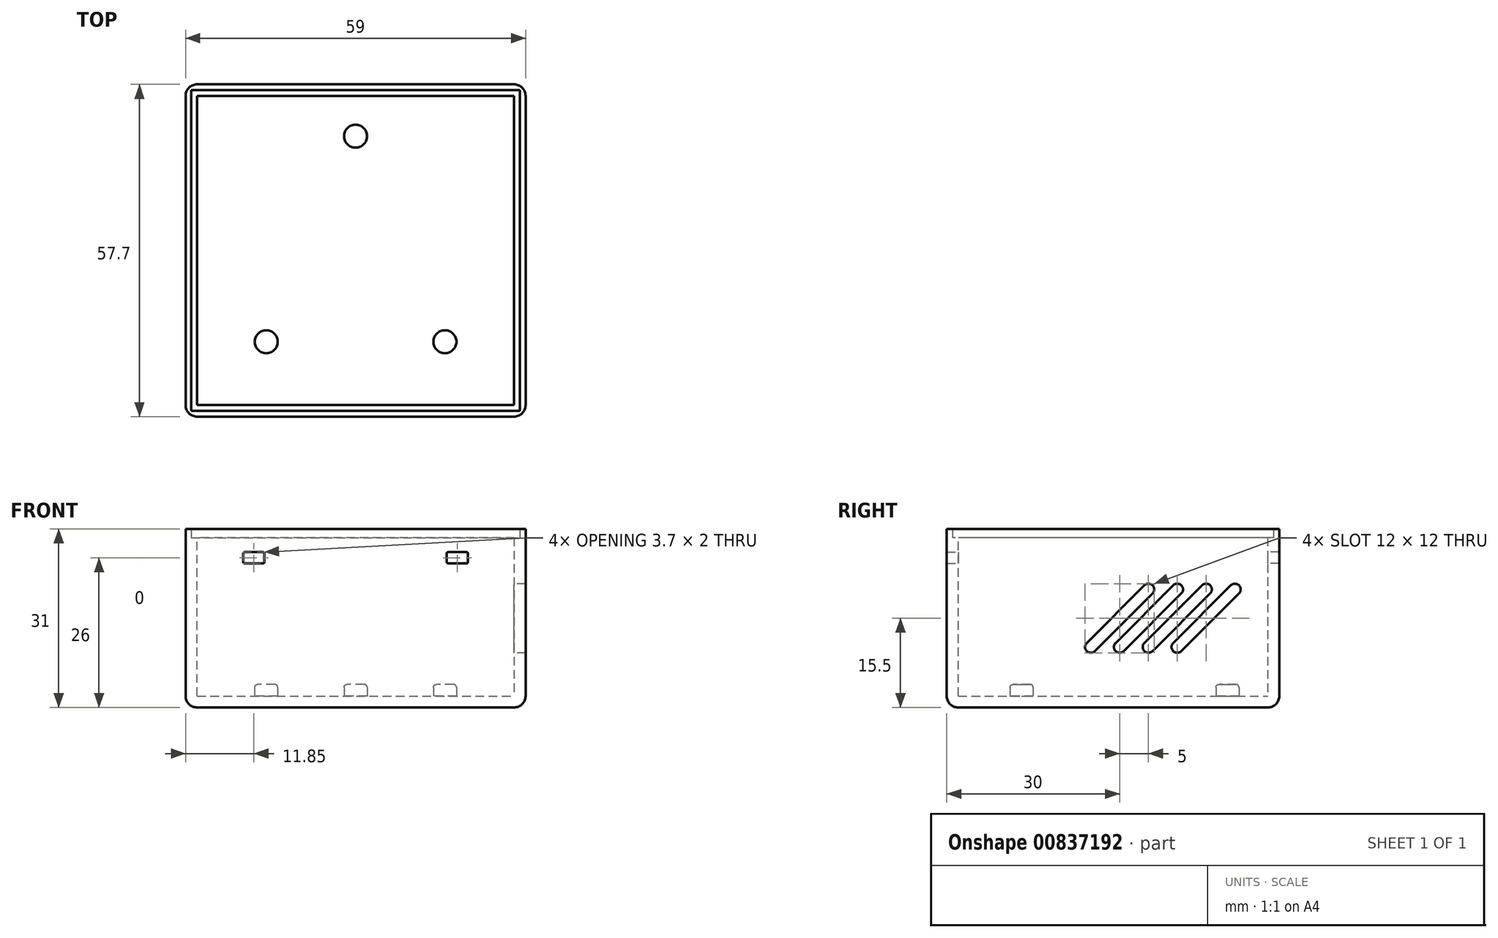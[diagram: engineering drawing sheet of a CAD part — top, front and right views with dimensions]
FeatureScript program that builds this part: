
annotation { "Feature Type Name" : "Feature", "Feature Type Description" : "" }
export const myFeature = defineFeature(function(context is Context, id is Id, definition is map)
    precondition{}
    {
        {
            var Q0;
            Q0=qCreatedBy(makeId("Top.planeOp"),FACE);
            var sketch = newSketch(context, id + "F0", { "sketchPlane" : qUnion([Q0])});
            skLineSegment(sketch, "E0", {"start": v(0, 0) * mm, "end": v(0, 53.7) * mm});
            skLineSegment(sketch, "E1", {"start": v(0, 53.7) * mm, "end": v(55, 53.7) * mm});
            skLineSegment(sketch, "E2", {"start": v(55, 53.7) * mm, "end": v(55, 0) * mm});
            skLineSegment(sketch, "E3", {"start": v(0, 0) * mm, "end": v(55, 0) * mm});
            skPoint(sketch, "E4.visualSharp", {"position": v(0, 53.7) * mm});
            skPoint(sketch, "E5.visualSharp", {"position": v(55, 53.7) * mm});
            skPoint(sketch, "E6.visualSharp", {"position": v(55, 0) * mm});
            skPoint(sketch, "E7.visualSharp", {"position": v(0, 0) * mm});
            skCircle(sketch, "E8", {"center": v(27.5, 46.7) * mm, "radius": 2 * mm});
            skPoint(sketch, "E9", {"position": v(27.5, 53.7) * mm});
            skCircle(sketch, "E10", {"center": v(12, 11) * mm, "radius": 2 * mm});
            skCircle(sketch, "E11", {"center": v(43, 11) * mm, "radius": 2 * mm});
            skLineSegment(sketch, "E12", {"start": v(27.5, 53.7) * mm, "end": v(27.5, 0) * mm, "construction": true});
            skPoint(sketch, "E13", {"position": v(12, 0) * mm});
            skPoint(sketch, "E14", {"position": v(43, 0) * mm});
            skSolve(sketch);
        }
        {
            var Q0;
            Q0=makeQuery(id+"F0.imprint","IMPRINT",FACE,{"disambiguationData":[TD([[makeQuery(id+"F0.imprint","IMPRINT",EDGE,{"derivedFrom":sQuery(id+"F0.wireOp",EDGE,"E0")}),-1.0]])]});
            extrude(context, id + "F1", {"entities" : qUnion([Q0]), "depth" : 2 * mm, "offsetDistance" : 25 * mm});
        }
        {
            var Q0;
            Q0=makeQuery(id+"F0.imprint","IMPRINT",FACE,{"disambiguationData":[TD([[makeQuery(id+"F0.imprint","IMPRINT",EDGE,{"derivedFrom":sQuery(id+"F0.wireOp",EDGE,"E10")}),1.0]])]});
            var Q1;
            Q1=makeQuery(id+"F0.imprint","IMPRINT",FACE,{"disambiguationData":[TD([[makeQuery(id+"F0.imprint","IMPRINT",EDGE,{"derivedFrom":sQuery(id+"F0.wireOp",EDGE,"E8")}),1.0]])]});
            var Q2;
            Q2=makeQuery(id+"F0.imprint","IMPRINT",FACE,{"disambiguationData":[TD([[makeQuery(id+"F0.imprint","IMPRINT",EDGE,{"derivedFrom":sQuery(id+"F0.wireOp",EDGE,"E11")}),1.0]])]});
            extrude(context, id + "F2", {"entities" : qUnion([Q0, Q1, Q2]), "operationType" : NewBodyOperationType.ADD, "depth" : 4 * mm, "offsetDistance" : 25 * mm});
        }
        {
            var Q0;
            Q0=makeQuery(id+"F1.opExtrude","SWEPT_FACE",FACE,{"disambiguationData":[OSD([sQuery(id+"F0.wireOp",EDGE,"E3")])]});
            var sketch = newSketch(context, id + "F3", { "sketchPlane" : qUnion([Q0])});
            skLineSegment(sketch, "E15", {"start": v(0, 0) * mm, "end": v(0, 31) * mm});
            skLineSegment(sketch, "E16", {"start": v(0, 31) * mm, "end": v(55, 31) * mm});
            skLineSegment(sketch, "E17", {"start": v(55, 31) * mm, "end": v(55, 0) * mm});
            skLineSegment(sketch, "E18.bottom", {"start": v(8, 27) * mm, "end": v(11.7, 27) * mm});
            skLineSegment(sketch, "E18.top", {"start": v(8, 25) * mm, "end": v(11.7, 25) * mm});
            skLineSegment(sketch, "E18.left", {"start": v(8, 27) * mm, "end": v(8, 25) * mm});
            skLineSegment(sketch, "E18.right", {"start": v(11.7, 27) * mm, "end": v(11.7, 25) * mm});
            skPoint(sketch, "E19", {"position": v(27.5, 31) * mm});
            skPoint(sketch, "E20", {"position": v(27.5, 0) * mm});
            skLineSegment(sketch, "E21", {"start": v(27.5, 31) * mm, "end": v(27.5, 0) * mm, "construction": true});
            skLineSegment(sketch, "E22.bottom", {"start": v(43.3, 27) * mm, "end": v(47, 27) * mm});
            skLineSegment(sketch, "E22.top", {"start": v(43.3, 25) * mm, "end": v(47, 25) * mm});
            skLineSegment(sketch, "E22.left", {"start": v(47, 27) * mm, "end": v(47, 25) * mm});
            skLineSegment(sketch, "E22.right", {"start": v(43.3, 27) * mm, "end": v(43.3, 25) * mm});
            skPoint(sketch, "E23", {"position": v(55, 29.5) * mm});
            skPoint(sketch, "E24", {"position": v(0, 29.5) * mm});
            skLineSegment(sketch, "E25", {"start": v(0, 29.5) * mm, "end": v(55, 29.5) * mm});
            skSolve(sketch);
        }
        {
            var Q0;
            Q0=makeQuery(id+"F3.imprint","IMPRINT",FACE,{"disambiguationData":[TD([[makeQuery(id+"F3.imprint","IMPRINT",EDGE,{"derivedFrom":sQuery(id+"F3.wireOp",EDGE,"E18.bottom")}),1.0]])]});
            var Q1;
            {var subQ1=sQuery(id+"F0.wireOp",EDGE,"E3");var subQ2=makeQuery(id+"F1.opExtrude","CAP_EDGE",EDGE,{"disambiguationData":[OSD([subQ1])],"isStart":true});Q1=makeQuery(id+"F3.imprint","IMPRINT",FACE,{"disambiguationData":[TD([[makeQuery(id+"F3.imprint","IMPRINT",EDGE,{"derivedFrom":subQ2}),1.0]])]});}
            extrude(context, id + "F4", {"entities" : qUnion([Q0, Q1]), "operationType" : NewBodyOperationType.ADD, "depth" : 2 * mm, "offsetDistance" : 25 * mm});
        }
        {
            var Q0;
            {var subQ0=sQuery(id+"F3.wireOp",EDGE,"E16");Q0=makeQuery(id+"F3.imprint","IMPRINT",FACE,{"disambiguationData":[TD([[makeQuery(id+"F3.imprint","IMPRINT",EDGE,{"derivedFrom":subQ0}),-1.0]])]});}
            extrude(context, id + "F5", {"entities" : qUnion([Q0]), "operationType" : NewBodyOperationType.ADD, "depth" : 2 * mm, "offsetDistance" : 25 * mm, "hasSecondDirection" : true, "secondDirectionOppositeDirection" : true, "secondDirectionDepth" : -1 * mm});
        }
        {
            var Q0;
            {var subQ0=sQuery(id+"F3.wireOp",EDGE,"E17");Q0=makeQuery(id+"F5.boolean.opBoolean","MERGE",FACE,{"derivedFrom":[makeQuery(id+"F4.boolean.opBoolean","MERGE",FACE,{"derivedFrom":[makeQuery(id+"F1.opExtrude","SWEPT_FACE",FACE,{"disambiguationData":[OSD([sQuery(id+"F0.wireOp",EDGE,"E2")])]}),makeQuery(id+"F4.opExtrude","SWEPT_FACE",FACE,{"disambiguationData":[OSD([subQ0])]})]}),makeQuery(id+"F5.opExtrude","SWEPT_FACE",FACE,{"disambiguationData":[OSD([subQ0])]})]});}
            var sketch = newSketch(context, id + "F6", { "sketchPlane" : qUnion([Q0])});
            skLineSegment(sketch, "E26", {"start": v(-2, 0) * mm, "end": v(-2, 31) * mm});
            skLineSegment(sketch, "E27", {"start": v(-2, 31) * mm, "end": v(53.7, 31) * mm});
            skLineSegment(sketch, "E28", {"start": v(53.7, 31) * mm, "end": v(53.7, 0) * mm});
            skPoint(sketch, "E29", {"position": v(53.7, 29.5) * mm});
            skPoint(sketch, "E30", {"position": v(-2, 29.5) * mm});
            skLineSegment(sketch, "E31", {"start": v(-2, 29.5) * mm, "end": v(53.7, 29.5) * mm});
            skCircle(sketch, "E32", {"center": v(23, 10.5) * mm, "radius": 1 * mm});
            skLineSegment(sketch, "E33.top", {"start": v(23, 20.5) * mm, "end": v(33, 20.5) * mm, "construction": true});
            skLineSegment(sketch, "E33.left", {"start": v(23, 10.5) * mm, "end": v(23, 20.5) * mm, "construction": true});
            skCircle(sketch, "E34", {"center": v(33, 20.5) * mm, "radius": 1 * mm});
            skLineSegment(sketch, "E35", {"start": v(22.3, 11.2) * mm, "end": v(32.3, 21.2) * mm});
            skLineSegment(sketch, "E36", {"start": v(23.7, 9.8) * mm, "end": v(33.7, 19.8) * mm});
            skCircle(sketch, "E37", {"center": v(28, 10.5) * mm, "radius": 1 * mm});
            skCircle(sketch, "E38", {"center": v(38, 20.5) * mm, "radius": 1 * mm});
            skLineSegment(sketch, "E39", {"start": v(27.3, 11.2) * mm, "end": v(37.3, 21.2) * mm});
            skLineSegment(sketch, "E40", {"start": v(28.7, 9.8) * mm, "end": v(38.7, 19.8) * mm});
            skCircle(sketch, "E41", {"center": v(33, 10.5) * mm, "radius": 1 * mm});
            skCircle(sketch, "E42", {"center": v(43, 20.5) * mm, "radius": 1 * mm});
            skLineSegment(sketch, "E43", {"start": v(32.3, 11.2) * mm, "end": v(42.3, 21.2) * mm});
            skLineSegment(sketch, "E44", {"start": v(33.7, 9.8) * mm, "end": v(43.7, 19.8) * mm});
            skLineSegment(sketch, "E45", {"start": v(23, 10.5) * mm, "end": v(28, 10.5) * mm, "construction": true});
            skLineSegment(sketch, "E46", {"start": v(28, 10.5) * mm, "end": v(33, 10.5) * mm, "construction": true});
            skCircle(sketch, "E47", {"center": v(38, 10.5) * mm, "radius": 1 * mm});
            skCircle(sketch, "E48", {"center": v(48, 20.5) * mm, "radius": 1 * mm});
            skLineSegment(sketch, "E49", {"start": v(37.3, 11.2) * mm, "end": v(47.3, 21.2) * mm});
            skLineSegment(sketch, "E50", {"start": v(38.7, 9.8) * mm, "end": v(48.7, 19.8) * mm});
            skLineSegment(sketch, "E51", {"start": v(33, 10.5) * mm, "end": v(38, 10.5) * mm, "construction": true});
            skLineSegment(sketch, "E52", {"start": v(33, 20.5) * mm, "end": v(33, 31) * mm, "construction": true});
            skLineSegment(sketch, "E53", {"start": v(23, 10.5) * mm, "end": v(23, 0) * mm, "construction": true});
            skSolve(sketch);
        }
        {
            var Q0;
            {var subQ6=sQuery(id+"F0.wireOp",EDGE,"E2");var subQ9=makeQuery(id+"F1.opExtrude","CAP_EDGE",EDGE,{"disambiguationData":[OSD([subQ6])],"isStart":false});Q0=makeQuery(id+"F6.imprint","IMPRINT",FACE,{"disambiguationData":[TD([[makeQuery(id+"F6.imprint","IMPRINT",EDGE,{"derivedFrom":subQ9}),1.0]])]});}
            var Q1;
            {var subQ2=sQuery(id+"F6.wireOp",EDGE,"E35");Q1=makeQuery(id+"F6.imprint","IMPRINT",FACE,{"disambiguationData":[TD([[makeQuery(id+"F6.imprint","IMPRINT",EDGE,{"derivedFrom":subQ2}),1.0]])]});}
            extrude(context, id + "F7", {"entities" : qUnion([Q0, Q1]), "operationType" : NewBodyOperationType.ADD, "depth" : 2 * mm, "offsetDistance" : 25 * mm});
        }
        {
            var Q0;
            {var subQ1=sQuery(id+"F3.wireOp",EDGE,"E17");var subQ5=makeQuery(id+"F5.opExtrude","CAP_EDGE",EDGE,{"disambiguationData":[OSD([subQ1])],"isStart":true});Q0=makeQuery(id+"F6.imprint","IMPRINT",FACE,{"disambiguationData":[TD([[makeQuery(id+"F6.imprint","IMPRINT",EDGE,{"derivedFrom":subQ5}),1.0]])]});}
            extrude(context, id + "F8", {"entities" : qUnion([Q0]), "operationType" : NewBodyOperationType.ADD, "depth" : 2 * mm, "offsetDistance" : 25 * mm, "hasSecondDirection" : true, "secondDirectionOppositeDirection" : true, "secondDirectionDepth" : -1 * mm});
        }
        {
            var Q0;
            Q0=makeQuery(id+"F7.boolean.opBoolean","MERGE",FACE,{"derivedFrom":[makeQuery(id+"F4.opExtrude","SWEPT_FACE",FACE,{"disambiguationData":[OSD([sQuery(id+"F3.wireOp",EDGE,"E25")])]}),makeQuery(id+"F7.opExtrude","SWEPT_FACE",FACE,{"disambiguationData":[OSD([sQuery(id+"F6.wireOp",EDGE,"E31")])]})]});
            var sketch = newSketch(context, id + "F9", { "sketchPlane" : qUnion([Q0])});
            skLineSegment(sketch, "E54", {"start": v(55, -1) * mm, "end": v(56, -1) * mm});
            skSolve(sketch);
        }
        {
            var Q0;
            Q0=makeQuery(id+"F9.imprint","IMPRINT",FACE,{"disambiguationData":[TD([[makeQuery(id+"F9.imprint","IMPRINT",EDGE,{"derivedFrom":sQuery(id+"F9.wireOp",EDGE,"E54")}),-1.0]])]});
            extrude(context, id + "F10", {"entities" : qUnion([Q0]), "operationType" : NewBodyOperationType.ADD, "depth" : 1.5 * mm, "offsetDistance" : 25 * mm});
        }
        {
            var Q0;
            {var subQ0=sQuery(id+"F6.wireOp",EDGE,"E28");Q0=makeQuery(id+"F8.boolean.opBoolean","MERGE",FACE,{"derivedFrom":[makeQuery(id+"F7.boolean.opBoolean","MERGE",FACE,{"derivedFrom":[makeQuery(id+"F1.opExtrude","SWEPT_FACE",FACE,{"disambiguationData":[OSD([sQuery(id+"F0.wireOp",EDGE,"E1")])]}),makeQuery(id+"F7.opExtrude","SWEPT_FACE",FACE,{"disambiguationData":[OSD([subQ0])]})]}),makeQuery(id+"F8.opExtrude","SWEPT_FACE",FACE,{"disambiguationData":[OSD([subQ0])]})]});}
            var sketch = newSketch(context, id + "F11", { "sketchPlane" : qUnion([Q0])});
            skLineSegment(sketch, "E55", {"start": v(-57, 0) * mm, "end": v(-57, 31) * mm});
            skLineSegment(sketch, "E56", {"start": v(-57, 0) * mm, "end": v(0, 0) * mm});
            skLineSegment(sketch, "E57", {"start": v(-57, 31) * mm, "end": v(0, 31) * mm});
            skLineSegment(sketch, "E58", {"start": v(0, 31) * mm, "end": v(0, 0) * mm});
            skPoint(sketch, "E59", {"position": v(0, 29.5) * mm});
            skPoint(sketch, "E60", {"position": v(-57, 29.5) * mm});
            skLineSegment(sketch, "E61", {"start": v(-57, 29.5) * mm, "end": v(0, 29.5) * mm});
            skPoint(sketch, "E62", {"position": v(-27.5, 2) * mm});
            skLineSegment(sketch, "E63", {"start": v(-27.5, 2) * mm, "end": v(-27.5, 29.5) * mm, "construction": true});
            skLineSegment(sketch, "E64.bottom", {"start": v(-47, 27) * mm, "end": v(-43.3, 27) * mm});
            skLineSegment(sketch, "E64.top", {"start": v(-47, 25) * mm, "end": v(-43.3, 25) * mm});
            skLineSegment(sketch, "E64.left", {"start": v(-47, 27) * mm, "end": v(-47, 25) * mm});
            skLineSegment(sketch, "E64.right", {"start": v(-43.3, 27) * mm, "end": v(-43.3, 25) * mm});
            skLineSegment(sketch, "E65.bottom", {"start": v(-11.7, 27) * mm, "end": v(-8, 27) * mm});
            skLineSegment(sketch, "E65.top", {"start": v(-11.7, 25) * mm, "end": v(-8, 25) * mm});
            skLineSegment(sketch, "E65.left", {"start": v(-11.7, 27) * mm, "end": v(-11.7, 25) * mm});
            skLineSegment(sketch, "E65.right", {"start": v(-8, 27) * mm, "end": v(-8, 25) * mm});
            skSolve(sketch);
        }
        {
            var Q0;
            Q0=makeQuery(id+"F11.imprint","IMPRINT",FACE,{"disambiguationData":[TD([[makeQuery(id+"F11.imprint","IMPRINT",EDGE,{"derivedFrom":sQuery(id+"F11.wireOp",EDGE,"E64.bottom")}),1.0]])]});
            var Q1;
            {var subQ7=sQuery(id+"F11.wireOp",EDGE,"E56");Q1=makeQuery(id+"F11.imprint","IMPRINT",FACE,{"disambiguationData":[TD([[makeQuery(id+"F11.imprint","IMPRINT",EDGE,{"derivedFrom":subQ7}),-1.0]])]});}
            extrude(context, id + "F12", {"entities" : qUnion([Q0, Q1]), "operationType" : NewBodyOperationType.ADD, "depth" : 2 * mm, "offsetDistance" : 25 * mm});
        }
        {
            var Q0;
            {var subQ1=sQuery(id+"F6.wireOp",EDGE,"E28");var subQ5=makeQuery(id+"F8.opExtrude","CAP_EDGE",EDGE,{"disambiguationData":[OSD([subQ1])],"isStart":true});Q0=makeQuery(id+"F11.imprint","IMPRINT",FACE,{"disambiguationData":[TD([[makeQuery(id+"F11.imprint","IMPRINT",EDGE,{"derivedFrom":subQ5}),1.0]])]});}
            extrude(context, id + "F13", {"entities" : qUnion([Q0]), "operationType" : NewBodyOperationType.ADD, "depth" : 2 * mm, "offsetDistance" : 25 * mm, "hasSecondDirection" : true, "secondDirectionOppositeDirection" : true, "secondDirectionDepth" : -1 * mm});
        }
        {
            var Q0;
            Q0=makeQuery(id+"F12.boolean.opBoolean","MERGE",FACE,{"derivedFrom":[makeQuery(id+"F7.boolean.opBoolean","MERGE",FACE,{"derivedFrom":[makeQuery(id+"F4.opExtrude","SWEPT_FACE",FACE,{"disambiguationData":[OSD([sQuery(id+"F3.wireOp",EDGE,"E25")])]}),makeQuery(id+"F7.opExtrude","SWEPT_FACE",FACE,{"disambiguationData":[OSD([sQuery(id+"F6.wireOp",EDGE,"E31")])]})]}),makeQuery(id+"F12.opExtrude","SWEPT_FACE",FACE,{"disambiguationData":[OSD([sQuery(id+"F11.wireOp",EDGE,"E61")])]})]});
            var sketch = newSketch(context, id + "F14", { "sketchPlane" : qUnion([Q0])});
            skLineSegment(sketch, "E66", {"start": v(56, 53.7) * mm, "end": v(56, 55.7) * mm});
            skLineSegment(sketch, "E67", {"start": v(56, 55.7) * mm, "end": v(57, 55.7) * mm});
            skLineSegment(sketch, "E68", {"start": v(57, 55.7) * mm, "end": v(57, 53.7) * mm});
            skLineSegment(sketch, "E69", {"start": v(57, 53.7) * mm, "end": v(56, 53.7) * mm});
            skSolve(sketch);
        }
        {
            var Q0;
            {var subQ0=sQuery(id+"F14.wireOp",EDGE,"E67");Q0=makeQuery(id+"F14.imprint","IMPRINT",FACE,{"disambiguationData":[TD([[makeQuery(id+"F14.imprint","IMPRINT",EDGE,{"derivedFrom":subQ0}),1.0]])]});}
            extrude(context, id + "F15", {"entities" : qUnion([Q0]), "operationType" : NewBodyOperationType.ADD, "depth" : 1.5 * mm, "offsetDistance" : 25 * mm});
        }
        {
            var Q0;
            {var subQ0=sQuery(id+"F11.wireOp",EDGE,"E58");var subQ1=sQuery(id+"F3.wireOp",EDGE,"E15");var subQ2=sQuery(id+"F0.wireOp",EDGE,"E3");Q0=makeQuery(id+"F13.boolean.opBoolean","MERGE",FACE,{"derivedFrom":[makeQuery(id+"F12.boolean.opBoolean","MERGE",FACE,{"derivedFrom":[makeQuery(id+"F4.boolean.opBoolean","MERGE",FACE,{"derivedFrom":[makeQuery(id+"F1.opExtrude","SWEPT_FACE",FACE,{"disambiguationData":[OSD([sQuery(id+"F0.wireOp",EDGE,"E0")])]}),makeQuery(id+"F4.opExtrude","SWEPT_FACE",FACE,{"disambiguationData":[OSD([subQ1]),TDD([makeQuery(id+"F3.imprint","IMPRINT",EDGE,{"disambiguationData":[TD([[makeQuery(id+"F3.imprint","INTERSECT",VERTEX,{"derivedFrom":[makeQuery(id+"F1.opExtrude","CAP_EDGE",EDGE,{"disambiguationData":[OSD([subQ2])],"isStart":true}),subQ1]}),1.0]])],"derivedFrom":subQ1})])]})]}),makeQuery(id+"F12.opExtrude","SWEPT_FACE",FACE,{"disambiguationData":[OSD([subQ0])]})]}),makeQuery(id+"F13.opExtrude","SWEPT_FACE",FACE,{"disambiguationData":[OSD([subQ0])]})]});}
            var sketch = newSketch(context, id + "F16", { "sketchPlane" : qUnion([Q0])});
            skLineSegment(sketch, "E70", {"start": v(-55.7, 0) * mm, "end": v(2, 0) * mm});
            skLineSegment(sketch, "E71", {"start": v(2, 0) * mm, "end": v(2, 31) * mm});
            skLineSegment(sketch, "E72", {"start": v(2, 31) * mm, "end": v(-55.7, 31) * mm});
            skLineSegment(sketch, "E73", {"start": v(-55.7, 31) * mm, "end": v(-55.7, 0) * mm});
            skPoint(sketch, "E74", {"position": v(-55.7, 29.5) * mm});
            skPoint(sketch, "E75", {"position": v(2, 29.5) * mm});
            skLineSegment(sketch, "E76", {"start": v(-55.7, 29.5) * mm, "end": v(2, 29.5) * mm});
            skSolve(sketch);
        }
        {
            var Q0;
            Q0=makeQuery(id+"F16.imprint","IMPRINT",FACE,{"disambiguationData":[TD([[makeQuery(id+"F16.imprint","IMPRINT",EDGE,{"derivedFrom":makeQuery(id+"F1.opExtrude","CAP_EDGE",EDGE,{"disambiguationData":[OSD([sQuery(id+"F0.wireOp",EDGE,"E0")])],"isStart":false})}),-1.0]])]});
            var Q1;
            Q1=makeQuery(id+"F16.imprint","IMPRINT",FACE,{"disambiguationData":[TD([[makeQuery(id+"F16.imprint","IMPRINT",EDGE,{"derivedFrom":makeQuery(id+"F1.opExtrude","CAP_EDGE",EDGE,{"disambiguationData":[OSD([sQuery(id+"F0.wireOp",EDGE,"E0")])],"isStart":false})}),1.0]])]});
            extrude(context, id + "F17", {"entities" : qUnion([Q0, Q1]), "operationType" : NewBodyOperationType.ADD, "depth" : 2 * mm, "offsetDistance" : 25 * mm});
        }
        {
            var Q0;
            {var subQ1=sQuery(id+"F11.wireOp",EDGE,"E58");var subQ3=makeQuery(id+"F13.opExtrude","CAP_EDGE",EDGE,{"disambiguationData":[OSD([subQ1])],"isStart":true});Q0=makeQuery(id+"F16.imprint","IMPRINT",FACE,{"disambiguationData":[TD([[makeQuery(id+"F16.imprint","IMPRINT",EDGE,{"derivedFrom":subQ3}),1.0]])]});}
            extrude(context, id + "F18", {"entities" : qUnion([Q0]), "operationType" : NewBodyOperationType.ADD, "depth" : 2 * mm, "offsetDistance" : 25 * mm, "hasSecondDirection" : true, "secondDirectionOppositeDirection" : true, "secondDirectionDepth" : -1 * mm});
        }
        {
            var Q0;
            Q0=makeQuery(id+"F17.boolean.opBoolean","MERGE",FACE,{"derivedFrom":[makeQuery(id+"F12.boolean.opBoolean","MERGE",FACE,{"derivedFrom":[makeQuery(id+"F7.boolean.opBoolean","MERGE",FACE,{"derivedFrom":[makeQuery(id+"F4.opExtrude","SWEPT_FACE",FACE,{"disambiguationData":[OSD([sQuery(id+"F3.wireOp",EDGE,"E25")])]}),makeQuery(id+"F7.opExtrude","SWEPT_FACE",FACE,{"disambiguationData":[OSD([sQuery(id+"F6.wireOp",EDGE,"E31")])]})]}),makeQuery(id+"F12.opExtrude","SWEPT_FACE",FACE,{"disambiguationData":[OSD([sQuery(id+"F11.wireOp",EDGE,"E61")])]})]}),makeQuery(id+"F17.opExtrude","SWEPT_FACE",FACE,{"disambiguationData":[OSD([sQuery(id+"F16.wireOp",EDGE,"E76")])]})]});
            var sketch = newSketch(context, id + "F19", { "sketchPlane" : qUnion([Q0])});
            skLineSegment(sketch, "E77", {"start": v(0, 55.7) * mm, "end": v(0, 54.7) * mm});
            skLineSegment(sketch, "E78", {"start": v(0, 54.7) * mm, "end": v(-2, 54.7) * mm});
            skLineSegment(sketch, "E79", {"start": v(-2, 54.7) * mm, "end": v(-2, 55.7) * mm});
            skLineSegment(sketch, "E80", {"start": v(-2, 55.7) * mm, "end": v(0, 55.7) * mm});
            skSolve(sketch);
        }
        {
            var Q0;
            {var subQ3=sQuery(id+"F19.wireOp",EDGE,"E77");Q0=makeQuery(id+"F19.imprint","IMPRINT",FACE,{"disambiguationData":[TD([[makeQuery(id+"F19.imprint","IMPRINT",EDGE,{"derivedFrom":subQ3}),-1.0]])]});}
            extrude(context, id + "F20", {"entities" : qUnion([Q0]), "operationType" : NewBodyOperationType.ADD, "depth" : 1.5 * mm, "offsetDistance" : 25 * mm});
        }
        {
            var Q0;
            Q0=makeQuery(id+"F17.boolean.opBoolean","MERGE",FACE,{"derivedFrom":[makeQuery(id+"F12.boolean.opBoolean","MERGE",FACE,{"derivedFrom":[makeQuery(id+"F7.boolean.opBoolean","MERGE",FACE,{"derivedFrom":[makeQuery(id+"F4.opExtrude","SWEPT_FACE",FACE,{"disambiguationData":[OSD([sQuery(id+"F3.wireOp",EDGE,"E25")])]}),makeQuery(id+"F7.opExtrude","SWEPT_FACE",FACE,{"disambiguationData":[OSD([sQuery(id+"F6.wireOp",EDGE,"E31")])]})]}),makeQuery(id+"F12.opExtrude","SWEPT_FACE",FACE,{"disambiguationData":[OSD([sQuery(id+"F11.wireOp",EDGE,"E61")])]})]}),makeQuery(id+"F17.opExtrude","SWEPT_FACE",FACE,{"disambiguationData":[OSD([sQuery(id+"F16.wireOp",EDGE,"E76")])]})]});
            var sketch = newSketch(context, id + "F21", { "sketchPlane" : qUnion([Q0])});
            skLineSegment(sketch, "E81", {"start": v(0, -2) * mm, "end": v(-1, -2) * mm});
            skLineSegment(sketch, "E82", {"start": v(-1, -2) * mm, "end": v(-1, -1) * mm});
            skLineSegment(sketch, "E83", {"start": v(-1, -1) * mm, "end": v(0, -1) * mm});
            skLineSegment(sketch, "E84", {"start": v(0, -1) * mm, "end": v(0, -2) * mm});
            skSolve(sketch);
        }
        {
            var Q0;
            Q0=makeQuery(id+"F21.imprint","IMPRINT",FACE,{"disambiguationData":[TD([[makeQuery(id+"F21.imprint","IMPRINT",EDGE,{"derivedFrom":sQuery(id+"F21.wireOp",EDGE,"E81")}),1.0]])]});
            extrude(context, id + "F22", {"entities" : qUnion([Q0]), "operationType" : NewBodyOperationType.ADD, "depth" : 1.5 * mm, "offsetDistance" : 25 * mm});
        }
        {
            var Q0;
            Q0=makeQuery(id+"F4.opExtrude","SWEPT_EDGE",EDGE,{"disambiguationData":[OSD([sQuery(id+"F3.wireOp",EDGE,"E18.bottom"),sQuery(id+"F3.wireOp",EDGE,"E18.left")])]});
            var Q1;
            Q1=makeQuery(id+"F4.opExtrude","SWEPT_EDGE",EDGE,{"disambiguationData":[OSD([sQuery(id+"F3.wireOp",EDGE,"E18.bottom"),sQuery(id+"F3.wireOp",EDGE,"E18.right")])]});
            var Q2;
            Q2=makeQuery(id+"F4.opExtrude","SWEPT_EDGE",EDGE,{"disambiguationData":[OSD([sQuery(id+"F3.wireOp",EDGE,"E18.top"),sQuery(id+"F3.wireOp",EDGE,"E18.left")])]});
            var Q3;
            Q3=makeQuery(id+"F4.opExtrude","SWEPT_EDGE",EDGE,{"disambiguationData":[OSD([sQuery(id+"F3.wireOp",EDGE,"E18.top"),sQuery(id+"F3.wireOp",EDGE,"E18.right")])]});
            var Q4;
            Q4=makeQuery(id+"F4.opExtrude","SWEPT_EDGE",EDGE,{"disambiguationData":[OSD([sQuery(id+"F3.wireOp",EDGE,"E22.top"),sQuery(id+"F3.wireOp",EDGE,"E22.right")])]});
            var Q5;
            Q5=makeQuery(id+"F4.opExtrude","SWEPT_EDGE",EDGE,{"disambiguationData":[OSD([sQuery(id+"F3.wireOp",EDGE,"E22.top"),sQuery(id+"F3.wireOp",EDGE,"E22.left")])]});
            var Q6;
            Q6=makeQuery(id+"F4.opExtrude","SWEPT_EDGE",EDGE,{"disambiguationData":[OSD([sQuery(id+"F3.wireOp",EDGE,"E22.bottom"),sQuery(id+"F3.wireOp",EDGE,"E22.right")])]});
            var Q7;
            Q7=makeQuery(id+"F4.opExtrude","SWEPT_EDGE",EDGE,{"disambiguationData":[OSD([sQuery(id+"F3.wireOp",EDGE,"E22.bottom"),sQuery(id+"F3.wireOp",EDGE,"E22.left")])]});
            var Q8;
            Q8=makeQuery(id+"F12.opExtrude","SWEPT_EDGE",EDGE,{"disambiguationData":[OSD([sQuery(id+"F11.wireOp",EDGE,"E64.bottom"),sQuery(id+"F11.wireOp",EDGE,"E64.left")])]});
            var Q9;
            Q9=makeQuery(id+"F12.opExtrude","SWEPT_EDGE",EDGE,{"disambiguationData":[OSD([sQuery(id+"F11.wireOp",EDGE,"E64.top"),sQuery(id+"F11.wireOp",EDGE,"E64.right")])]});
            var Q10;
            Q10=makeQuery(id+"F12.opExtrude","SWEPT_EDGE",EDGE,{"disambiguationData":[OSD([sQuery(id+"F11.wireOp",EDGE,"E64.bottom"),sQuery(id+"F11.wireOp",EDGE,"E64.right")])]});
            var Q11;
            Q11=makeQuery(id+"F12.opExtrude","SWEPT_EDGE",EDGE,{"disambiguationData":[OSD([sQuery(id+"F11.wireOp",EDGE,"E64.top"),sQuery(id+"F11.wireOp",EDGE,"E64.left")])]});
            var Q12;
            Q12=makeQuery(id+"F12.opExtrude","SWEPT_EDGE",EDGE,{"disambiguationData":[OSD([sQuery(id+"F11.wireOp",EDGE,"E65.top"),sQuery(id+"F11.wireOp",EDGE,"E65.left")])]});
            var Q13;
            Q13=makeQuery(id+"F12.opExtrude","SWEPT_EDGE",EDGE,{"disambiguationData":[OSD([sQuery(id+"F11.wireOp",EDGE,"E65.top"),sQuery(id+"F11.wireOp",EDGE,"E65.right")])]});
            var Q14;
            Q14=makeQuery(id+"F12.opExtrude","SWEPT_EDGE",EDGE,{"disambiguationData":[OSD([sQuery(id+"F11.wireOp",EDGE,"E65.bottom"),sQuery(id+"F11.wireOp",EDGE,"E65.left")])]});
            var Q15;
            Q15=makeQuery(id+"F12.opExtrude","SWEPT_EDGE",EDGE,{"disambiguationData":[OSD([sQuery(id+"F11.wireOp",EDGE,"E65.bottom"),sQuery(id+"F11.wireOp",EDGE,"E65.right")])]});
            fillet(context, id + "F23", {"entities" : qUnion([Q0, Q1, Q2, Q3, Q4, Q5, Q6, Q7, Q8, Q9, Q10, Q11, Q12, Q13, Q14, Q15]), "radius" : 0.3 * mm, "tangentPropagation" : true, "allowEdgeOverflow" : false});
        }
        {
            var Q0;
            Q0=makeQuery(id+"F12.boolean.opBoolean","MERGE",EDGE,{"derivedFrom":[makeQuery(id+"F7.opExtrude","CAP_EDGE",EDGE,{"disambiguationData":[OSD([sQuery(id+"F0.wireOp",EDGE,"E2"),sQuery(id+"F0.wireOp",EDGE,"E3"),sQuery(id+"F3.wireOp",EDGE,"E17")])],"isStart":false}),makeQuery(id+"F12.opExtrude","SWEPT_EDGE",EDGE,{"disambiguationData":[OSD([sQuery(id+"F11.wireOp",EDGE,"E55"),sQuery(id+"F11.wireOp",EDGE,"E56")])]})]});
            var Q1;
            Q1=makeQuery(id+"F17.boolean.opBoolean","MERGE",EDGE,{"derivedFrom":[makeQuery(id+"F12.opExtrude","CAP_EDGE",EDGE,{"disambiguationData":[OSD([sQuery(id+"F11.wireOp",EDGE,"E56")])],"isStart":false}),makeQuery(id+"F17.opExtrude","SWEPT_EDGE",EDGE,{"disambiguationData":[OSD([sQuery(id+"F16.wireOp",EDGE,"E70"),sQuery(id+"F16.wireOp",EDGE,"E73")])]})]});
            var Q2;
            {var subQ0=sQuery(id+"F0.wireOp",EDGE,"E3");Q2=makeQuery(id+"F7.boolean.opBoolean","MERGE",EDGE,{"derivedFrom":[makeQuery(id+"F4.opExtrude","CAP_EDGE",EDGE,{"disambiguationData":[OSD([subQ0])],"isStart":false}),makeQuery(id+"F7.opExtrude","SWEPT_EDGE",EDGE,{"disambiguationData":[OSD([sQuery(id+"F0.wireOp",EDGE,"E2"),subQ0,sQuery(id+"F3.wireOp",EDGE,"E17"),sQuery(id+"F6.wireOp",EDGE,"E26")])]})]});}
            var Q3;
            {var subQ0=sQuery(id+"F16.wireOp",EDGE,"E70");Q3=makeQuery(id+"F17.opExtrude","CAP_EDGE",EDGE,{"disambiguationData":[OSD([subQ0]),TDD([makeQuery(id+"F16.imprint","IMPRINT",EDGE,{"disambiguationData":[TD([[makeQuery(id+"F16.imprint","INTERSECT",VERTEX,{"derivedFrom":[subQ0,sQuery(id+"F16.wireOp",EDGE,"E73")]}),1.0]])],"derivedFrom":subQ0})])],"isStart":false});}
            var Q4;
            {var subQ0=sQuery(id+"F6.wireOp",EDGE,"E31");var subQ1=sQuery(id+"F6.wireOp",EDGE,"E26");Q4=makeQuery(id+"F10.boolean.opBoolean","MERGE",EDGE,{"derivedFrom":[makeQuery(id+"F7.opExtrude","CAP_EDGE",EDGE,{"disambiguationData":[OSD([subQ1])],"isStart":false}),makeQuery(id+"F10.opExtrude","SWEPT_EDGE",EDGE,{"disambiguationData":[OSD([subQ1,subQ0]),TDD([makeQuery(id+"F9.imprint","INTERSECT",VERTEX,{"derivedFrom":[makeQuery(id+"F7.opExtrude","SWEPT_EDGE",EDGE,{"disambiguationData":[OSD([subQ1,subQ0])]}),makeQuery(id+"F7.opExtrude","CAP_EDGE",EDGE,{"disambiguationData":[OSD([subQ0])],"isStart":false})]})])]})]});}
            var Q5;
            Q5=makeQuery(id+"F15.boolean.opBoolean","MERGE",EDGE,{"derivedFrom":[makeQuery(id+"F12.opExtrude","CAP_EDGE",EDGE,{"disambiguationData":[OSD([sQuery(id+"F11.wireOp",EDGE,"E55")])],"isStart":false}),makeQuery(id+"F15.opExtrude","SWEPT_EDGE",EDGE,{"disambiguationData":[OSD([sQuery(id+"F14.wireOp",EDGE,"E67"),sQuery(id+"F14.wireOp",EDGE,"E68")])]})]});
            var Q6;
            Q6=makeQuery(id+"F20.boolean.opBoolean","MERGE",EDGE,{"derivedFrom":[makeQuery(id+"F17.opExtrude","CAP_EDGE",EDGE,{"disambiguationData":[OSD([sQuery(id+"F16.wireOp",EDGE,"E73")])],"isStart":false}),makeQuery(id+"F20.opExtrude","SWEPT_EDGE",EDGE,{"disambiguationData":[OSD([sQuery(id+"F19.wireOp",EDGE,"E79"),sQuery(id+"F19.wireOp",EDGE,"E80")])]})]});
            var Q7;
            {var subQ0=sQuery(id+"F16.wireOp",EDGE,"E71");Q7=makeQuery(id+"F18.boolean.opBoolean","MERGE",EDGE,{"derivedFrom":[makeQuery(id+"F17.opExtrude","CAP_EDGE",EDGE,{"disambiguationData":[OSD([subQ0]),TDD([makeQuery(id+"F16.imprint","IMPRINT",EDGE,{"disambiguationData":[TD([[makeQuery(id+"F16.imprint","INTERSECT",VERTEX,{"derivedFrom":[subQ0,sQuery(id+"F16.wireOp",EDGE,"E76")]}),1.0]])],"derivedFrom":subQ0})])],"isStart":false}),makeQuery(id+"F18.opExtrude","CAP_EDGE",EDGE,{"disambiguationData":[OSD([subQ0])],"isStart":false})]});}
            fillet(context, id + "F24", {"entities" : qUnion([Q0, Q1, Q2, Q3, Q4, Q5, Q6, Q7]), "radius" : 2 * mm, "tangentPropagation" : true, "allowEdgeOverflow" : false});
        }
        {
            var Q0;
            Q0=makeQuery(id+"F2.opExtrude","CAP_EDGE",EDGE,{"disambiguationData":[OSD([sQuery(id+"F0.wireOp",EDGE,"E10")])],"isStart":false});
            var Q1;
            Q1=makeQuery(id+"F2.opExtrude","CAP_EDGE",EDGE,{"disambiguationData":[OSD([sQuery(id+"F0.wireOp",EDGE,"E8")])],"isStart":false});
            var Q2;
            Q2=makeQuery(id+"F2.opExtrude","CAP_EDGE",EDGE,{"disambiguationData":[OSD([sQuery(id+"F0.wireOp",EDGE,"E11")])],"isStart":false});
            fillet(context, id + "F25", {"entities" : qUnion([Q0, Q1, Q2]), "radius" : .5 * mm, "tangentPropagation" : true, "allowEdgeOverflow" : false});
        }
    });
